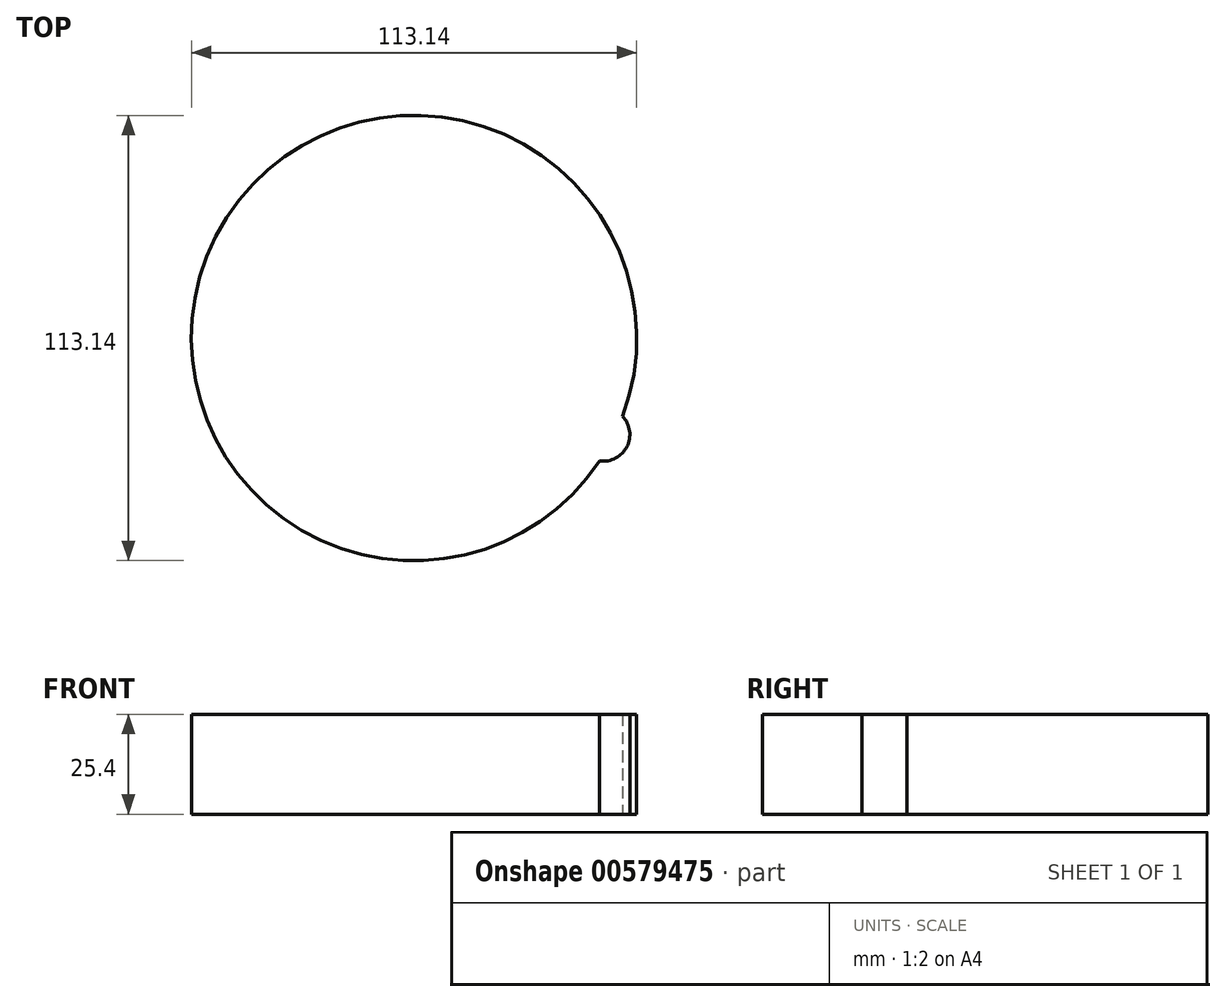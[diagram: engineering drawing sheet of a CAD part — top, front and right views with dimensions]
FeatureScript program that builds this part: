
annotation { "Feature Type Name" : "Feature", "Feature Type Description" : "" }
export const myFeature = defineFeature(function(context is Context, id is Id, definition is map)
    precondition{}
    {
        {
            var Q0;
            Q0=qCreatedBy(makeId("Top.planeOp"),FACE);
            var sketch = newSketch(context, id + "F0", { "sketchPlane" : qUnion([Q0])});
            skCircle(sketch, "E0", {"center": v(-66.4, -8.43) * mm, "radius": 56.57 * mm});
            skCircle(sketch, "E1", {"center": v(-18.34, -32.96) * mm, "radius": 6.77 * mm});
            skSolve(sketch);
        }
        {
            var Q0;
            Q0 = qSketchRegion(id + "F0", true);
            extrude(context, id + "F1", {"entities" : qUnion([Q0]), "depth" : 25.4 * mm, "offsetDistance" : 25.4 * mm});
        }
    });
